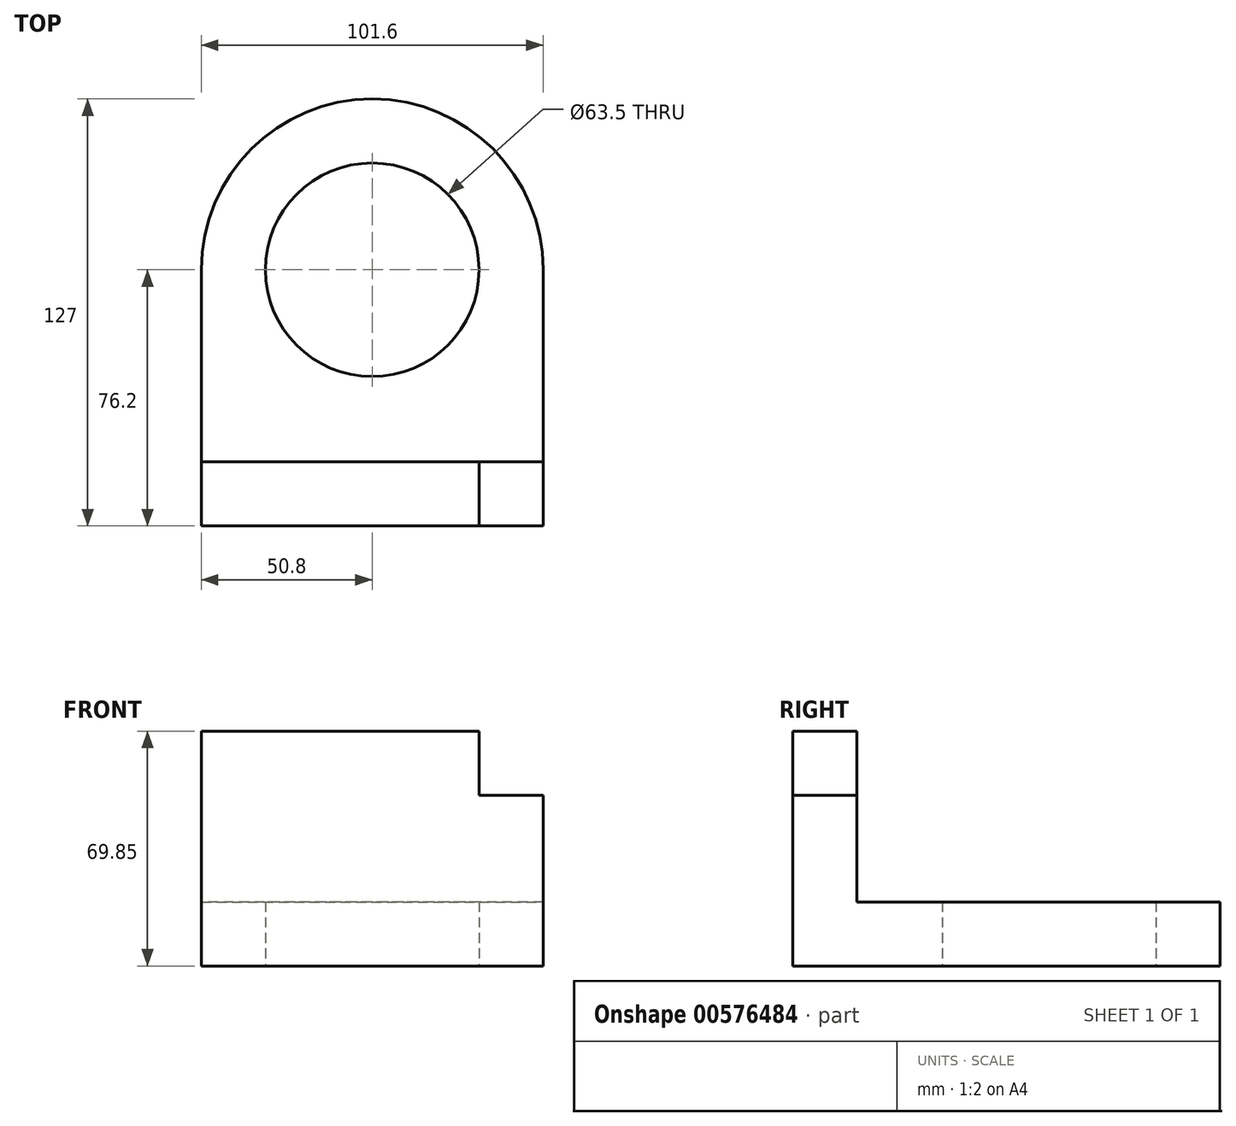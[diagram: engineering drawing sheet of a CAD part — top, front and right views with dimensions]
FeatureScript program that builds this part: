
annotation { "Feature Type Name" : "Feature", "Feature Type Description" : "" }
export const myFeature = defineFeature(function(context is Context, id is Id, definition is map)
    precondition{}
    {
        {
            var Q0;
            Q0=qCreatedBy(makeId("Top.planeOp"),FACE);
            var sketch = newSketch(context, id + "F0", { "sketchPlane" : qUnion([Q0])});
            skLineSegment(sketch, "E0.bottom", {"start": v(50.8, 63.5) * mm, "end": v(-50.8, 63.5) * mm});
            skLineSegment(sketch, "E0.top", {"start": v(50.8, -63.5) * mm, "end": v(-50.8, -63.5) * mm});
            skLineSegment(sketch, "E0.left", {"start": v(50.8, 63.5) * mm, "end": v(50.8, -63.5) * mm});
            skLineSegment(sketch, "E0.right", {"start": v(-50.8, 63.5) * mm, "end": v(-50.8, -63.5) * mm});
            skPoint(sketch, "E0.middle", {"position": v(0, 0) * mm});
            skArc(sketch, "E1", {"start": v(50.8, 12.7) * mm, "mid": v(0, 63.5) * mm, "end": v(-50.8, 12.7) * mm});
            skCircle(sketch, "E2", {"center": v(0, 12.7) * mm, "radius": 31.75 * mm});
            skSolve(sketch);
        }
        {
            var Q0;
            {var subQ1=sQuery(id+"F0.wireOp",EDGE,"E0.top");Q0=makeQuery(id+"F0.imprint","IMPRINT",FACE,{"disambiguationData":[TD([[makeQuery(id+"F0.imprint","IMPRINT",EDGE,{"derivedFrom":subQ1}),-1.0]])]});}
            extrude(context, id + "F1", {"entities" : qUnion([Q0]), "depth" : 19.05 * mm, "offsetDistance" : 25.4 * mm});
        }
        {
            var Q0;
            Q0=makeQuery(id+"F1.opExtrude","CAP_FACE",FACE,{"disambiguationData":[OSD([sQuery(id+"F0.wireOp",EDGE,"E0.top"),sQuery(id+"F0.wireOp",EDGE,"E0.left"),sQuery(id+"F0.wireOp",EDGE,"E0.right"),sQuery(id+"F0.wireOp",EDGE,"E1"),sQuery(id+"F0.wireOp",EDGE,"E2")])],"isStart":false});
            var sketch = newSketch(context, id + "F2", { "sketchPlane" : qUnion([Q0])});
            skLineSegment(sketch, "E3.bottom", {"start": v(-50.8, -63.5) * mm, "end": v(50.8, -63.5) * mm});
            skLineSegment(sketch, "E3.top", {"start": v(-50.8, -44.45) * mm, "end": v(50.8, -44.45) * mm});
            skLineSegment(sketch, "E3.left", {"start": v(-50.8, -63.5) * mm, "end": v(-50.8, -44.45) * mm});
            skLineSegment(sketch, "E3.right", {"start": v(50.8, -63.5) * mm, "end": v(50.8, -44.45) * mm});
            skSolve(sketch);
        }
        {
            var Q0;
            Q0=makeQuery(id+"F2.imprint","IMPRINT",FACE,{"disambiguationData":[TD([[makeQuery(id+"F2.imprint","IMPRINT",EDGE,{"derivedFrom":sQuery(id+"F2.wireOp",EDGE,"E3.bottom")}),-1.0]])]});
            extrude(context, id + "F3", {"entities" : qUnion([Q0]), "operationType" : NewBodyOperationType.ADD, "depth" : 50.8 * mm, "offsetDistance" : 25.4 * mm});
        }
        {
            var Q0;
            Q0=makeQuery(id+"F3.opExtrude","CAP_FACE",FACE,{"disambiguationData":[OSD([sQuery(id+"F2.wireOp",EDGE,"E3.bottom"),sQuery(id+"F2.wireOp",EDGE,"E3.top"),sQuery(id+"F2.wireOp",EDGE,"E3.left"),sQuery(id+"F2.wireOp",EDGE,"E3.right")])],"isStart":false});
            var sketch = newSketch(context, id + "F4", { "sketchPlane" : qUnion([Q0])});
            skLineSegment(sketch, "E4.bottom", {"start": v(50.8, -44.45) * mm, "end": v(31.75, -44.45) * mm});
            skLineSegment(sketch, "E4.top", {"start": v(50.8, -63.5) * mm, "end": v(31.75, -63.5) * mm});
            skLineSegment(sketch, "E4.left", {"start": v(50.8, -44.45) * mm, "end": v(50.8, -63.5) * mm});
            skLineSegment(sketch, "E4.right", {"start": v(31.75, -44.45) * mm, "end": v(31.75, -63.5) * mm});
            skSolve(sketch);
        }
        {
            var Q0;
            Q0=makeQuery(id+"F4.imprint","IMPRINT",FACE,{"disambiguationData":[TD([[makeQuery(id+"F4.imprint","IMPRINT",EDGE,{"derivedFrom":sQuery(id+"F4.wireOp",EDGE,"E4.bottom")}),-1.0]])]});
            extrude(context, id + "F5", {"entities" : qUnion([Q0]), "operationType" : NewBodyOperationType.REMOVE, "oppositeDirection" : true, "depth" : 19.05 * mm, "offsetDistance" : 25.4 * mm});
        }
    });
